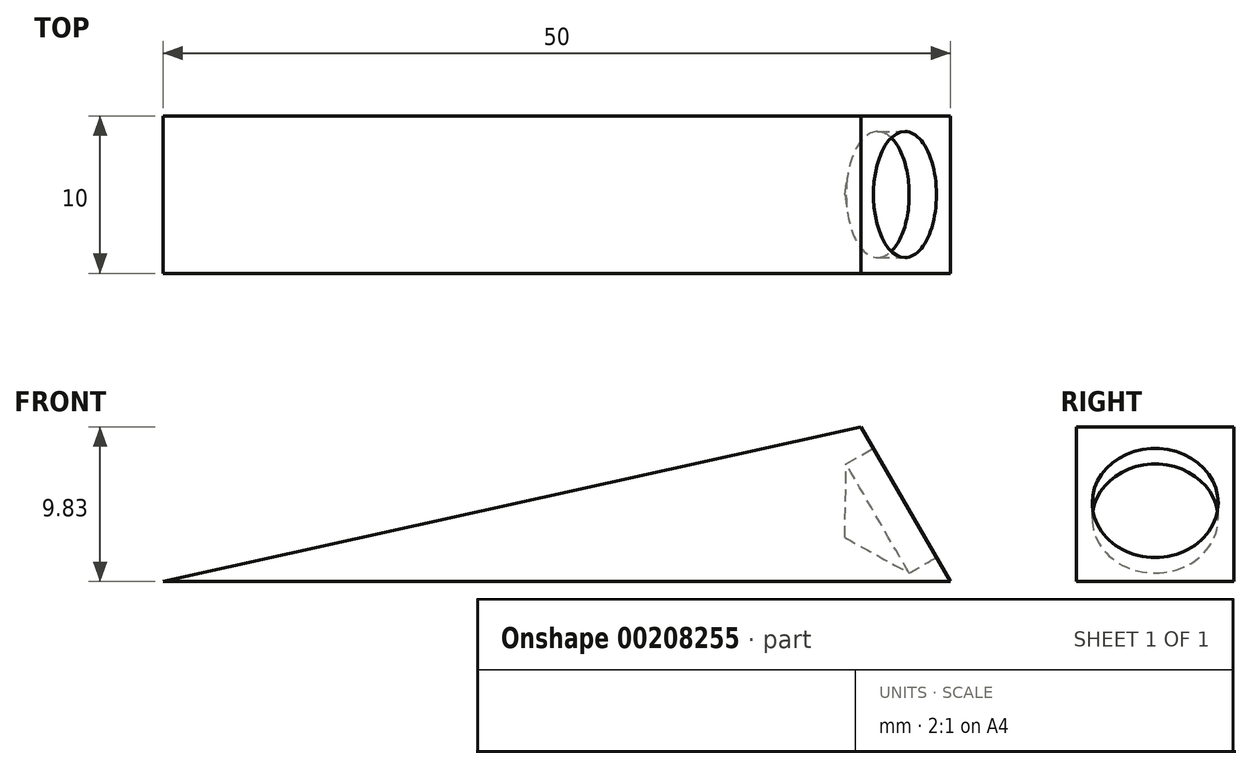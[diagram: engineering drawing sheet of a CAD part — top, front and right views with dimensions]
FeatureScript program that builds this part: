
annotation { "Feature Type Name" : "Feature", "Feature Type Description" : "" }
export const myFeature = defineFeature(function(context is Context, id is Id, definition is map)
    precondition{}
    {
        {
            var Q0;
            Q0=qCreatedBy(makeId("Top.planeOp"),FACE);
            var sketch = newSketch(context, id + "F0", { "sketchPlane" : qUnion([Q0])});
            skLineSegment(sketch, "E0", {"start": v(-46.65, 24.2) * mm, "end": v(3.35, 24.2) * mm});
            skLineSegment(sketch, "E1", {"start": v(3.35, 24.2) * mm, "end": v(3.35, 14.2) * mm});
            skLineSegment(sketch, "E2", {"start": v(3.35, 14.2) * mm, "end": v(-46.65, 14.2) * mm});
            skLineSegment(sketch, "E3", {"start": v(-46.65, 14.2) * mm, "end": v(-46.65, 24.2) * mm});
            skSolve(sketch);
        }
        {
            var Q0;
            Q0=makeQuery(id+"F0.imprint","IMPRINT",FACE,{"disambiguationData":[TD([[makeQuery(id+"F0.imprint","IMPRINT",EDGE,{"derivedFrom":sQuery(id+"F0.wireOp",EDGE,"E0")}),-1.0]])]});
            extrude(context, id + "F1", {"entities" : qUnion([Q0]), "depth" : 10 * mm});
        }
        {
            var Q0;
            Q0=makeQuery(id+"F1.opExtrude","CAP_EDGE",EDGE,{"disambiguationData":[OSD([sQuery(id+"F0.wireOp",EDGE,"E1")])],"isStart":false});
            chamfer(context, id + "F2", {"entities" : qUnion([Q0]), "chamferType" : ChamferType.OFFSET_ANGLE, "width" : 10 * mm, "oppositeDirection" : false, "angle" : 30 * degree, "tangentPropagation" : true});
        }
        {
            var Q0;
            Q0=makeQuery(id+"F2.opChamfer","BLEND_FACE",FACE,{"disambiguationData":[OSD([sQuery(id+"F0.wireOp",EDGE,"E1")])]});
            var sketch = newSketch(context, id + "F3", { "sketchPlane" : qUnion([Q0])});
            skCircle(sketch, "E4", {"center": v(19.2, 4.1) * mm, "radius": 4 * mm});
            skSolve(sketch);
        }
        {
            var Q0;
            Q0=sQuery(id+"F3.wireOp",VERTEX,"E4.center");
            var Q1;
            Q1=makeQuery(id+"F1.opExtrude","SWEPT_BODY",BODY,{"disambiguationData":[OSD([sQuery(id+"F0.wireOp",EDGE,"E0"),sQuery(id+"F0.wireOp",EDGE,"E1"),sQuery(id+"F0.wireOp",EDGE,"E2"),sQuery(id+"F0.wireOp",EDGE,"E3")])]});
            hole(context, id + "F4", {"style" : HoleStyle.SIMPLE, "endStyle" : HoleEndStyle.BLIND, "holeDiameter" : 8 * mm, "holeDepth" : 2 * mm, "locations" : qUnion([Q0]), "scope" : qUnion([Q1])});
        }
        {
            var Q0;
            Q0=makeQuery(id+"F1.opExtrude","CAP_EDGE",EDGE,{"disambiguationData":[OSD([sQuery(id+"F0.wireOp",EDGE,"E3")])],"isStart":false});
            chamfer(context, id + "F5", {"entities" : qUnion([Q0]), "chamferType" : ChamferType.OFFSET_ANGLE, "width" : 10 * mm, "oppositeDirection" : false, "angle" : 77.5 * degree, "tangentPropagation" : true});
        }
    });
